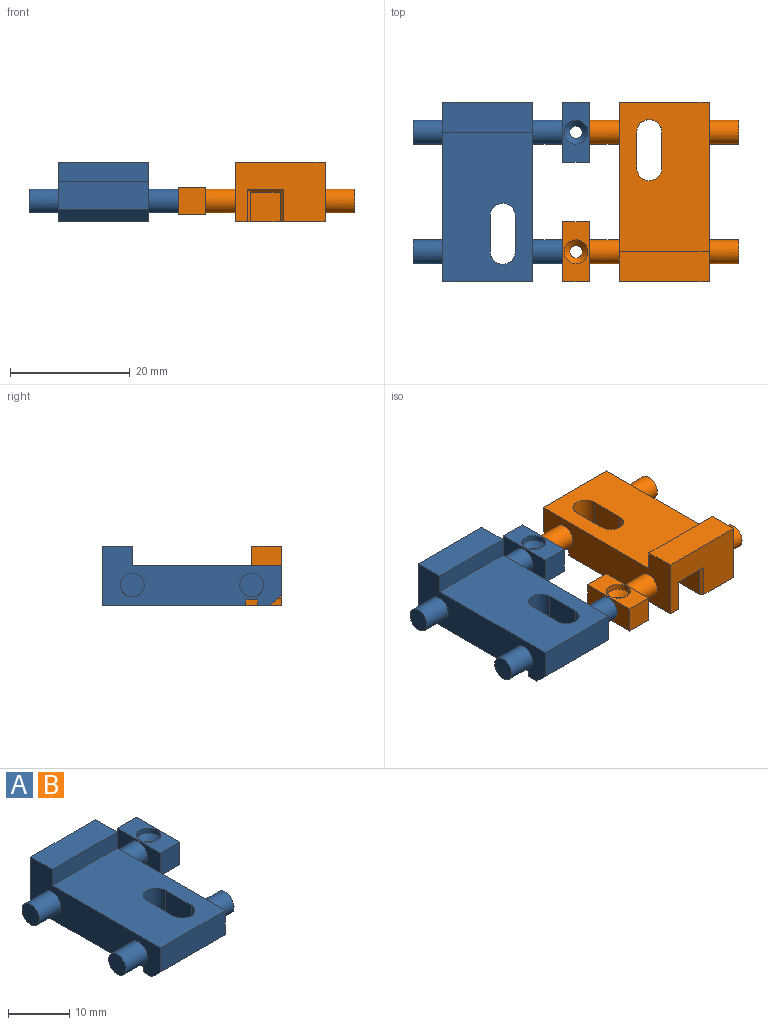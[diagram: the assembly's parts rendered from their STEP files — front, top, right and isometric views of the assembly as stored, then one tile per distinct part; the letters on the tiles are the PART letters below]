
ASSEMBLY  parts=2 mates=1
PART A: 43 faces, bbox 29.5x30x10 mm
  f0: cylinder r=1.05mm len=2.55mm, axis (0,0,-1), area 16.8mm2, adj f40,f42
  f1: plane 24x15mm, normal (0,0,-1), area 256.8mm2, adj f2,f3,f8,f18,f19,f20,f23,f26
  f2: plane 15x10mm, normal (0,1,0), area 117mm2, adj f1,f3,f8,f9,f32,f33,f34
  f3: plane 30x10mm, normal (-1,0,0), area 190.9mm2, adj f1,f2,f5,f6,f7,f9,f10,f12
  f4: cylinder r=2.1mm len=6.8mm, axis (0,0,1), area 42.8mm2, adj f5,f6,f18,f19,f22,f24,f25,f27
  f5: plane 15x2mm, normal (0,0,-1), area 27.1mm2, adj f3,f4,f8,f21,f24,f25
  f6: plane 25x15mm, normal (0,0,1), area 335.9mm2, adj f3,f4,f7,f8,f10,f18,f19,f20
  f7: plane 15x4.8mm, normal (0,-1,0), area 72mm2, adj f3,f6,f8,f21
  f8: plane 30x10mm, normal (1,0,0), area 190.9mm2, adj f1,f2,f5,f6,f7,f9,f10,f11
  f9: plane 15x5mm, normal (0,0,1), area 75mm2, adj f2,f3,f8,f10
  f10: plane 15x3.2mm, normal (0,-1,0), area 48mm2, adj f3,f6,f8,f9
  f11: cylinder r=2mm len=5mm, axis (-1,0,0), area 62.8mm2, adj f8,f36
  f12: cylinder r=2mm len=5mm, axis (-1,0,0), area 62.8mm2, adj f3,f13
  f13: plane 4x4mm, normal (-1,0,0), area 12.6mm2, adj f12
  f14: plane 4x4mm, normal (1,0,0), area 12.6mm2, adj f15
  f15: cylinder r=2mm len=5mm, axis (-1,0,0), area 62.8mm2, adj f8,f14
  f16: cylinder r=2mm len=5mm, axis (-1,0,0), area 62.8mm2, adj f3,f17
  f17: plane 4x4mm, normal (-1,0,0), area 12.6mm2, adj f16
  f18: plane 6.8x6mm, normal (1,0,0), area 39.8mm2, adj f1,f4,f6,f20,f26,f27
  f19: plane 6.8x6mm, normal (-1,0,0), area 39.8mm2, adj f1,f4,f6,f20,f22,f23
  f20: cylinder r=2.1mm len=6.8mm, axis (0,0,1), area 44.9mm2, adj f1,f6,f18,f19
  f21: plane 15x2mm, normal (0,-0.71,-0.71), area 42.4mm2, adj f3,f5,f7,f8
  f22: plane 3.15x2mm, normal (0,0,-1), area 5.9mm2, adj f4,f8,f19,f23,f24
  f23: plane 2.9x1mm, normal (0,-1,0), area 2.9mm2, adj f1,f8,f19,f22
  f24: plane 3.15x1mm, normal (0,1,0), area 3.2mm2, adj f4,f5,f8,f22
  f25: plane 8.15x1mm, normal (0,1,0), area 8.2mm2, adj f3,f4,f5,f27
  f26: plane 7.9x1mm, normal (0,-1,0), area 7.9mm2, adj f1,f3,f18,f27
  f27: plane 8.15x2mm, normal (0,0,-1), area 15.9mm2, adj f3,f4,f18,f25,f26
  f28: plane 5x5mm, normal (0,1,0), area 25mm2, adj f1,f29,f30,f31
  f29: plane 14.5x5mm, normal (1,0,0), area 72.5mm2, adj f1,f28,f31,f34
  f30: plane 14.5x5mm, normal (-1,0,0), area 72.5mm2, adj f1,f28,f31,f32
  f31: plane 14.5x5mm, normal (0,0,-1), area 72.5mm2, adj f28,f29,f30,f33
  f32: plane 5.5x0.5mm, normal (-0.71,0.71,0), area 3.7mm2, adj f1,f2,f30,f33
  f33: plane 6x0.5mm, normal (0,0.71,-0.71), area 3.9mm2, adj f2,f31,f32,f34
  f34: plane 5.5x0.5mm, normal (0.71,0.71,0), area 3.7mm2, adj f1,f2,f29,f33
  f35: plane 4.5x4.5mm, normal (0,1,0), area 20.2mm2, adj f36,f38,f39,f40
  f36: plane 10x4.5mm, normal (-1,0,0), area 32.4mm2, adj f11,f35,f37,f39,f40
  f37: plane 4.5x4.5mm, normal (0,-1,0), area 20.2mm2, adj f36,f38,f39,f40
  f38: plane 10x4.5mm, normal (1,0,0), area 45mm2, adj f35,f37,f39,f40
  f39: plane 10x4.5mm, normal (0,0,1), area 32.4mm2, adj f35,f36,f37,f38,f41
  f40: plane 10x4.5mm, normal (0,0,-1), area 41.5mm2, adj f0,f35,f36,f37,f38
  f41: cylinder r=2mm len=4mm, axis (0,0,1), area 12.6mm2, adj f39,f42
  f42: cone r=1.05mm half-angle=45deg, axis (0,0,1), area 12.9mm2, adj f0,f41
PART B: same geometry as A
PLACE A t=(-0.87,-2.01,-17.84)mm
PLACE B rot(axis=(0,0,1),180deg) t=(28.63,-2.01,-17.84)mm
MATE fastened A.f15 <-> B.f11  axis (-1,0,0) through (11.63,-12.01,-14.34)mm
